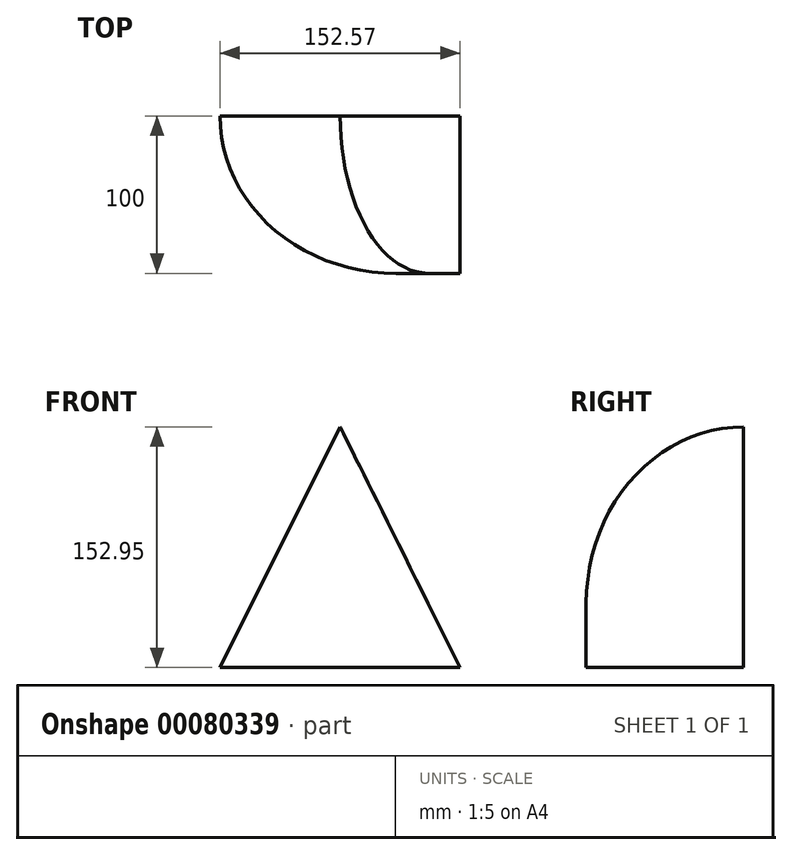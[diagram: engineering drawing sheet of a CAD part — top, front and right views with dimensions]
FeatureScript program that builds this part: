
annotation { "Feature Type Name" : "Feature", "Feature Type Description" : "" }
export const myFeature = defineFeature(function(context is Context, id is Id, definition is map)
    precondition{}
    {
        {
            var Q0;
            Q0=qCreatedBy(makeId("Front.planeOp"),FACE);
            var sketch = newSketch(context, id + "F0", { "sketchPlane" : qUnion([Q0])});
            skLineSegment(sketch, "E0", {"start": v(0, 76.4) * mm, "end": v(76.29, -76.54) * mm});
            skLineSegment(sketch, "E1", {"start": v(76.29, -76.54) * mm, "end": v(-76.28, -76.54) * mm});
            skLineSegment(sketch, "E2", {"start": v(-76.28, -76.54) * mm, "end": v(0, 76.4) * mm});
            skSolve(sketch);
        }
        {
            var Q0;
            Q0=makeQuery(id+"F0.imprint","IMPRINT",FACE,{"disambiguationData":[TD([[makeQuery(id+"F0.imprint","IMPRINT",EDGE,{"derivedFrom":sQuery(id+"F0.wireOp",EDGE,"E0")}),-1.0]])]});
            extrude(context, id + "F1", {"entities" : qUnion([Q0]), "depth" : 100 * mm});
        }
        {
            var Q0;
            Q0=makeQuery(id+"F1.opExtrude","CAP_EDGE",EDGE,{"disambiguationData":[OSD([sQuery(id+"F0.wireOp",EDGE,"E2")])],"isStart":false});
            fillet(context, id + "F2", {"entities" : qUnion([Q0]), "radius" : 100 * mm, "tangentPropagation" : true, "allowEdgeOverflow" : false});
        }
    });
